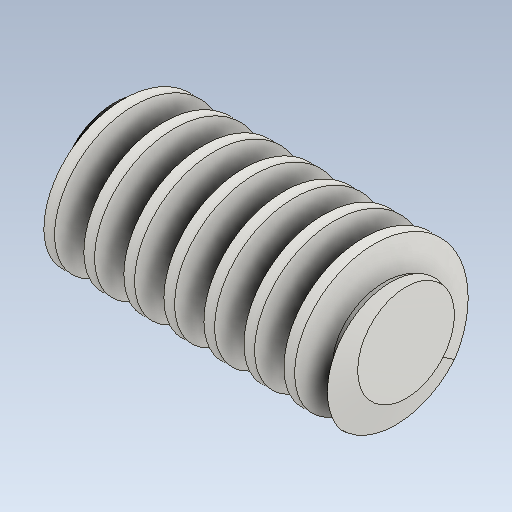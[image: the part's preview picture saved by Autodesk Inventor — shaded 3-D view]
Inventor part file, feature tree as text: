
AUTODESK INVENTOR PART (.ipt)
format: ipt  version: 2021 (Build 250183000, 183)  size: 427,520 bytes
history: native  units: mm (DEFAULTED — no unit token found)
features: other x6, chamfer x2, pattern_circular x2, extrude x1, sketch x1
ambient origin geometry x6: Origin, XZ Plane, X Axis, Y Axis, Z Axis, Center Point
bodies: Solid1 (feature_tree)
feature tree (12):
  extrude  "Base Body"  Depth=10.0mm
  chamfer  "Chamfer1"  Distance=38.1mm
  chamfer  "Chamfer2"  [1 undecoded]
  other  "Tooth Sketch"
  other  "Left Tooth"
  pattern_circular  "Left Tooth Pattern"  [2 undecoded]
  other  "Tooth"
  pattern_circular  "Tooth Pattern"  [2 undecoded]
  other  "Base Body Sketch"
  sketch  "Sketch5"  dims[d4=40.0mm d5=19.404171mm d6=38.1mm d7=0.0mm d8=1.294799mm d9=3.557431mm d10=1.294799mm d11=3.557431mm d12=19.198622mm d14=3.1425mm d24=19.198622mm d25=22.86mm d26=1.27mm d27=6.144654mm d28=8.085071mm d29=9.799106mm d30=5.08mm d31=10.0mm d32=100.0mm d33=0.0mm d34=90.0deg d35=90.0deg d36=0.0mm d37=0.0mm d43=10.0mm d45=360.0deg d46=45.0deg d47=45.0deg d49=0.0mm d53=0.0mm d54=80.850711mm d55=0.0mm d56=0.0mm d57=16.170142mm d58=25.4mm d59=0.0mm d60=5.08mm d61=25.4mm d62=100.0mm d63=0.0mm d64=90.0deg d65=90.0deg d66=0.0mm d67=0.0mm d68=10.0mm d69=10.0mm d70=360.0deg d72=10.0mm d74=10.0mm d75=10.0mm d76=0.0mm d77=80.850711mm]
  other  "Srf1"
  other  "Pitch Diameter"
note: 5 required parameter values undecoded (feature->parameter linkage not recoverable at this tier; creation-order binding heuristic only, values carry confidence <= 0.55)
